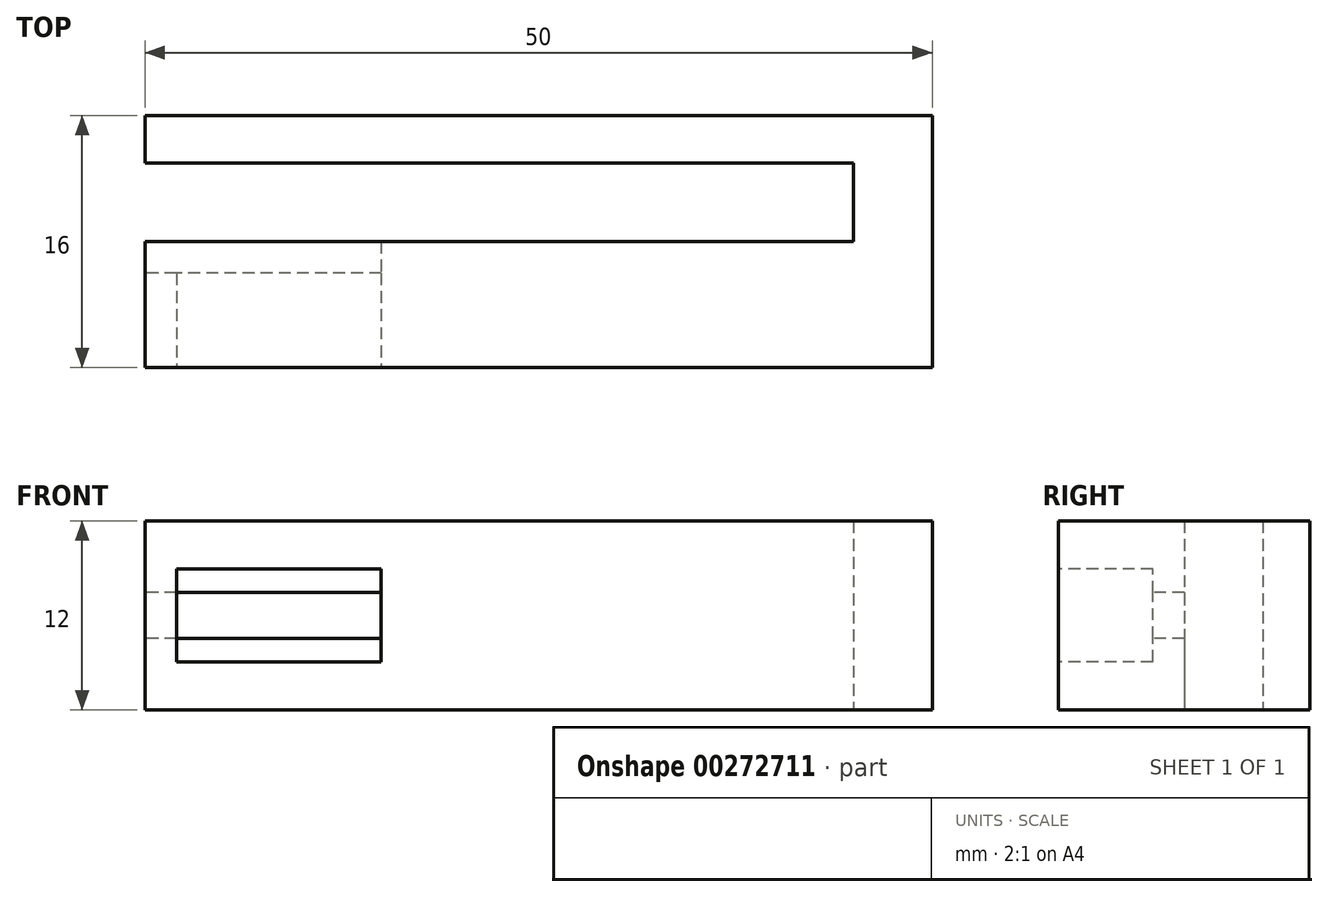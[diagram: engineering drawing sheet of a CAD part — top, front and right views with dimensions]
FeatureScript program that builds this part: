
annotation { "Feature Type Name" : "Feature", "Feature Type Description" : "" }
export const myFeature = defineFeature(function(context is Context, id is Id, definition is map)
    precondition{}
    {
        {
            var Q0;
            Q0=qCreatedBy(makeId("Top.planeOp"),FACE);
            var sketch = newSketch(context, id + "F0", { "sketchPlane" : qUnion([Q0])});
            skLineSegment(sketch, "E0", {"start": v(0, 0) * mm, "end": v(45, 0) * mm});
            skLineSegment(sketch, "E1", {"start": v(45, 0) * mm, "end": v(45, -5) * mm});
            skLineSegment(sketch, "E2", {"start": v(45, -5) * mm, "end": v(0, -5) * mm});
            skLineSegment(sketch, "E3", {"start": v(0, -5) * mm, "end": v(0, -13) * mm});
            skLineSegment(sketch, "E4", {"start": v(0, -13) * mm, "end": v(50, -13) * mm});
            skLineSegment(sketch, "E5", {"start": v(50, -13) * mm, "end": v(50, 3) * mm});
            skLineSegment(sketch, "E6", {"start": v(50, 3) * mm, "end": v(0, 3) * mm});
            skLineSegment(sketch, "E7", {"start": v(0, 3) * mm, "end": v(0, 0) * mm});
            skSolve(sketch);
        }
        {
            var Q0;
            Q0=makeQuery(id+"F0.imprint","IMPRINT",FACE,{"disambiguationData":[TD([[makeQuery(id+"F0.imprint","IMPRINT",EDGE,{"derivedFrom":sQuery(id+"F0.wireOp",EDGE,"E0")}),1.0]])]});
            extrude(context, id + "F1", {"entities" : qUnion([Q0]), "depth" : 12 * mm});
        }
        {
            var Q0;
            Q0=makeQuery(id+"F1.opExtrude","SWEPT_FACE",FACE,{"disambiguationData":[OSD([sQuery(id+"F0.wireOp",EDGE,"E4")])]});
            var sketch = newSketch(context, id + "F2", { "sketchPlane" : qUnion([Q0])});
            skLineSegment(sketch, "E8.bottom", {"start": v(15, 3.05) * mm, "end": v(2, 3.05) * mm});
            skLineSegment(sketch, "E8.top", {"start": v(15, 8.95) * mm, "end": v(2, 8.95) * mm});
            skLineSegment(sketch, "E8.left", {"start": v(15, 3.05) * mm, "end": v(15, 8.95) * mm});
            skLineSegment(sketch, "E8.right", {"start": v(2, 3.05) * mm, "end": v(2, 8.95) * mm});
            skPoint(sketch, "E9", {"position": v(15, 6) * mm});
            skSolve(sketch);
        }
        {
            var Q0;
            Q0=makeQuery(id+"F2.imprint","IMPRINT",FACE,{"disambiguationData":[TD([[makeQuery(id+"F2.imprint","IMPRINT",EDGE,{"derivedFrom":sQuery(id+"F2.wireOp",EDGE,"E8.bottom")}),-1.0]])]});
            extrude(context, id + "F3", {"entities" : qUnion([Q0]), "operationType" : NewBodyOperationType.REMOVE, "oppositeDirection" : true, "depth" : 6 * mm});
        }
        {
            var Q0;
            Q0=makeQuery(id+"F3.boolean.opBoolean","COPY",FACE,{"derivedFrom":makeQuery(id+"F3.opExtrude","CAP_FACE",FACE,{"disambiguationData":[OSD([sQuery(id+"F2.wireOp",EDGE,"E8.bottom"),sQuery(id+"F2.wireOp",EDGE,"E8.top"),sQuery(id+"F2.wireOp",EDGE,"E8.left"),sQuery(id+"F2.wireOp",EDGE,"E8.right")])],"isStart":false})});
            var sketch = newSketch(context, id + "F4", { "sketchPlane" : qUnion([Q0])});
            skLineSegment(sketch, "E10.bottom", {"start": v(15, 7.45) * mm, "end": v(2, 7.45) * mm});
            skLineSegment(sketch, "E10.top", {"start": v(15, 4.55) * mm, "end": v(2, 4.55) * mm});
            skLineSegment(sketch, "E10.left", {"start": v(15, 7.45) * mm, "end": v(15, 4.55) * mm});
            skLineSegment(sketch, "E10.right", {"start": v(2, 7.45) * mm, "end": v(2, 4.55) * mm});
            skSolve(sketch);
        }
        {
            var Q0;
            Q0=makeQuery(id+"F4.imprint","IMPRINT",FACE,{"disambiguationData":[TD([[makeQuery(id+"F4.imprint","IMPRINT",EDGE,{"derivedFrom":sQuery(id+"F4.wireOp",EDGE,"E10.bottom")}),1.0]])]});
            extrude(context, id + "F5", {"entities" : qUnion([Q0]), "operationType" : NewBodyOperationType.REMOVE, "endBound" : BoundingType.UP_TO_NEXT, "oppositeDirection" : true, "depth" : 25 * mm});
        }
        {
            var Q0;
            Q0=makeQuery(id+"F1.opExtrude","SWEPT_FACE",FACE,{"disambiguationData":[OSD([sQuery(id+"F0.wireOp",EDGE,"E3")])]});
            var sketch = newSketch(context, id + "F6", { "sketchPlane" : qUnion([Q0])});
            skLineSegment(sketch, "E11.0", {"start": v(5, 4.55) * mm, "end": v(7, 4.55) * mm});
            skLineSegment(sketch, "E12.0", {"start": v(5, 7.45) * mm, "end": v(7, 7.45) * mm});
            skLineSegment(sketch, "E13", {"start": v(7, 4.55) * mm, "end": v(7, 7.45) * mm});
            skLineSegment(sketch, "E14", {"start": v(5, 4.55) * mm, "end": v(5, 7.45) * mm});
            skSolve(sketch);
        }
        {
            var Q0;
            Q0=makeQuery(id+"F6.imprint","IMPRINT",FACE,{"disambiguationData":[TD([[makeQuery(id+"F6.imprint","IMPRINT",EDGE,{"derivedFrom":sQuery(id+"F6.wireOp",EDGE,"E11.0")}),1.0]])]});
            extrude(context, id + "F7", {"entities" : qUnion([Q0]), "operationType" : NewBodyOperationType.REMOVE, "endBound" : BoundingType.UP_TO_NEXT, "oppositeDirection" : true, "depth" : 25 * mm});
        }
    });
